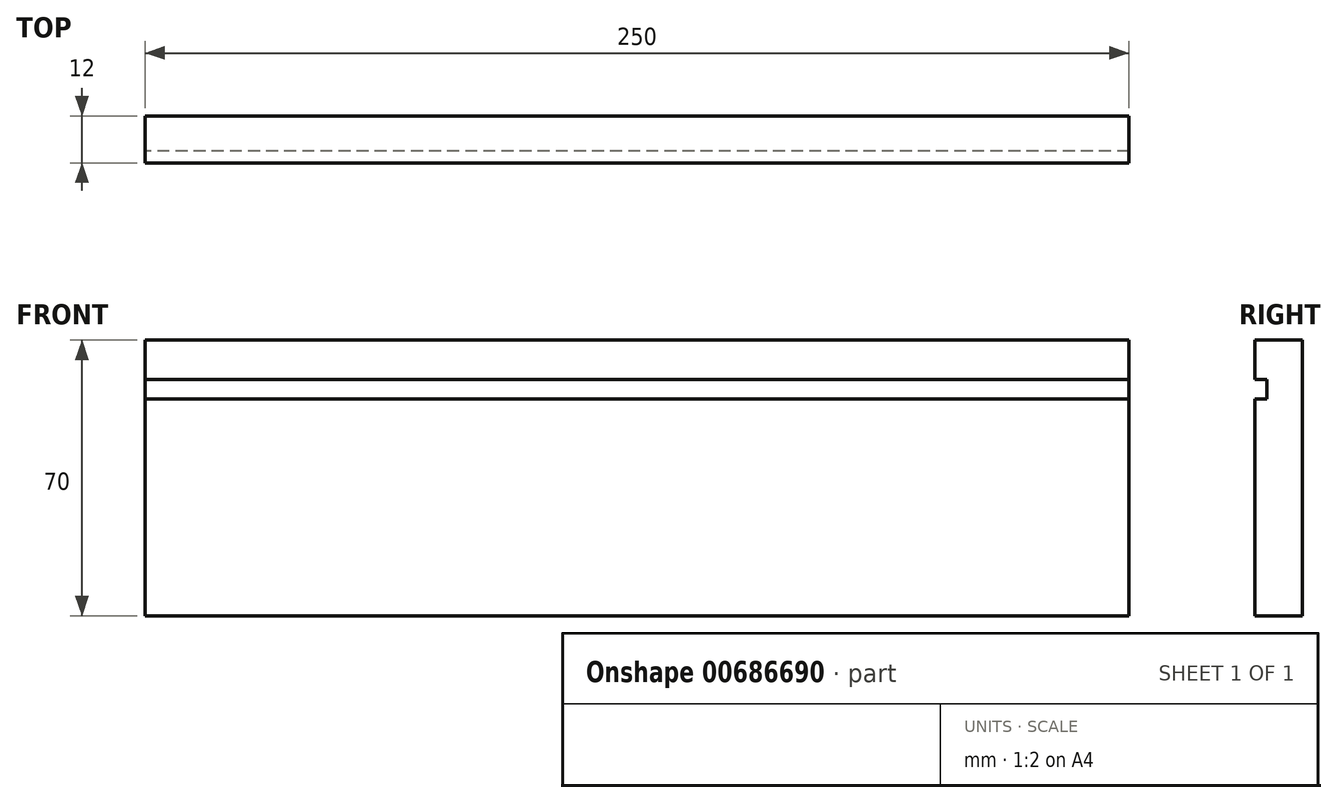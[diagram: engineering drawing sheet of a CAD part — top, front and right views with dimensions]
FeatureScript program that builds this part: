
annotation { "Feature Type Name" : "Feature", "Feature Type Description" : "" }
export const myFeature = defineFeature(function(context is Context, id is Id, definition is map)
    precondition{}
    {
        {
            var Q0;
            Q0=qCreatedBy(makeId("Right.planeOp"),FACE);
            var sketch = newSketch(context, id + "F0", { "sketchPlane" : qUnion([Q0])});
            skLineSegment(sketch, "E0.bottom", {"start": v(0, 0) * mm, "end": v(12, 0) * mm});
            skLineSegment(sketch, "E0.top", {"start": v(0, 70) * mm, "end": v(12, 70) * mm});
            skLineSegment(sketch, "E0.left", {"start": v(0, 0) * mm, "end": v(0, 55) * mm});
            skLineSegment(sketch, "E0.right", {"start": v(12, 0) * mm, "end": v(12, 70) * mm});
            skLineSegment(sketch, "E1.bottom", {"start": v(0, 60) * mm, "end": v(3, 60) * mm});
            skLineSegment(sketch, "E1.top", {"start": v(0, 55) * mm, "end": v(3, 55) * mm});
            skLineSegment(sketch, "E1.right", {"start": v(3, 60) * mm, "end": v(3, 55) * mm});
            skLineSegment(sketch, "E2.trimOffspring", {"start": v(0, 60) * mm, "end": v(0, 70) * mm});
            skSolve(sketch);
        }
        {
            var Q0;
            Q0=qSketchRegion(id+"F0",true);
            extrude(context, id + "F1", {"entities" : qUnion([Q0]), "depth" : 250 * mm, "offsetDistance" : 25 * mm});
        }
    });
